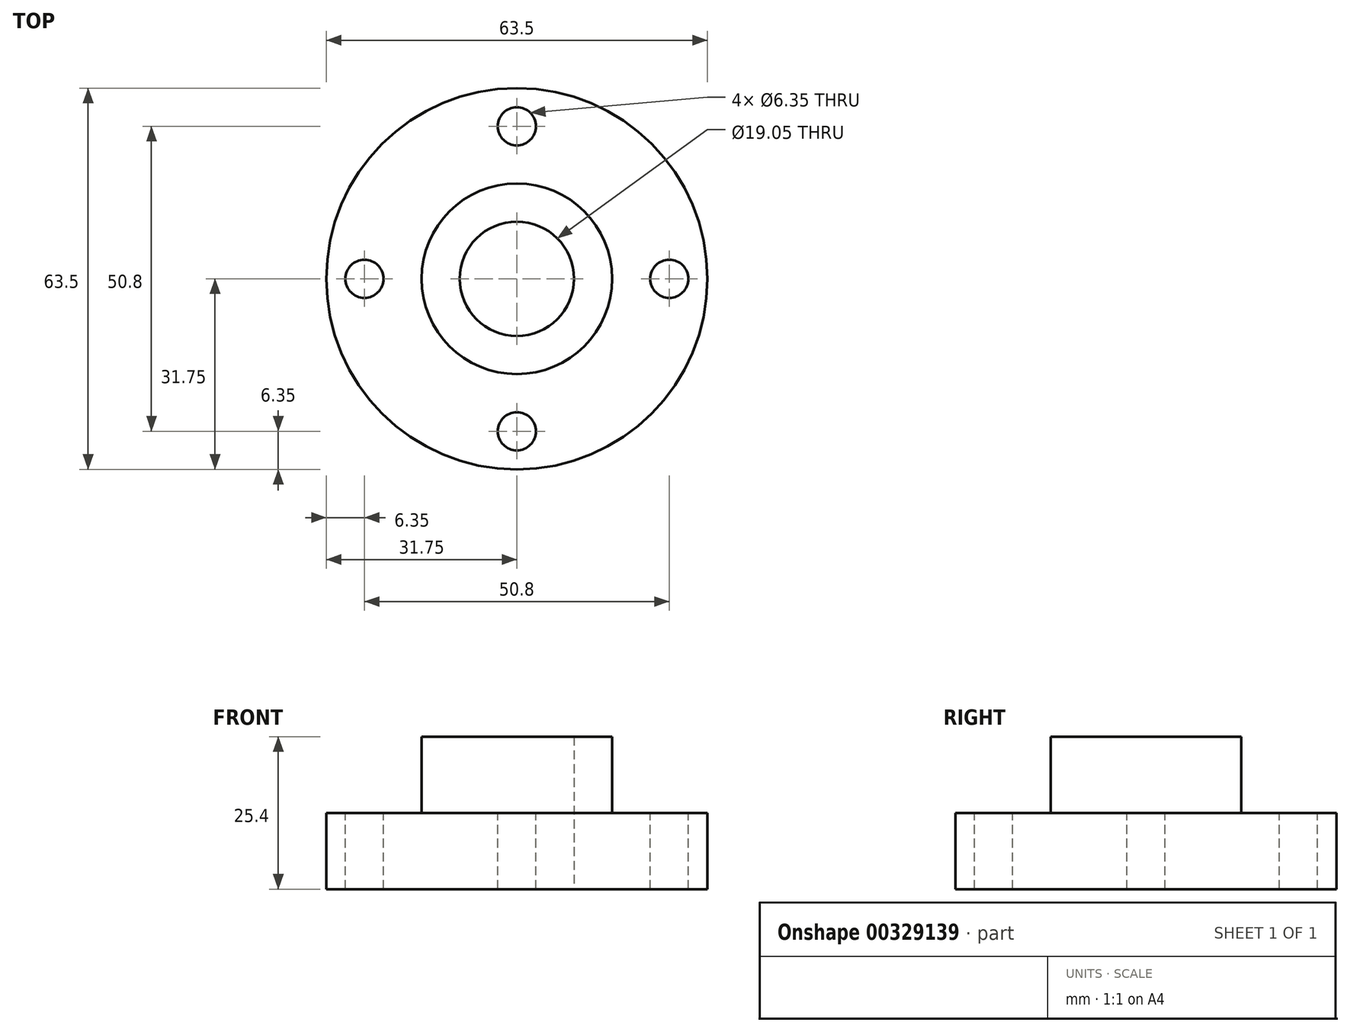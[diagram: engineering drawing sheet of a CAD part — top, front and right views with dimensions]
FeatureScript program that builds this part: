
annotation { "Feature Type Name" : "Feature", "Feature Type Description" : "" }
export const myFeature = defineFeature(function(context is Context, id is Id, definition is map)
    precondition{}
    {
        {
            var Q0;
            Q0=qCreatedBy(makeId("Top.planeOp"),FACE);
            var sketch = newSketch(context, id + "F0", { "sketchPlane" : qUnion([Q0])});
            skCircle(sketch, "E0", {"center": v(0, 0) * mm, "radius": 9.53 * mm});
            skCircle(sketch, "E1", {"center": v(0, 0) * mm, "radius": 15.88 * mm});
            skCircle(sketch, "E2", {"center": v(0, 0) * mm, "radius": 31.75 * mm});
            skSolve(sketch);
        }
        {
            var Q0;
            Q0=makeQuery(id+"F0.imprint","IMPRINT",FACE,{"disambiguationData":[TD([[makeQuery(id+"F0.imprint","IMPRINT",EDGE,{"derivedFrom":sQuery(id+"F0.wireOp",EDGE,"E0")}),-1.0]])]});
            extrude(context, id + "F1", {"entities" : qUnion([Q0]), "depth" : 25.4 * mm});
        }
        {
            var Q0;
            Q0=makeQuery(id+"F0.imprint","IMPRINT",FACE,{"disambiguationData":[TD([[makeQuery(id+"F0.imprint","IMPRINT",EDGE,{"derivedFrom":sQuery(id+"F0.wireOp",EDGE,"E1")}),-1.0]])]});
            extrude(context, id + "F2", {"entities" : qUnion([Q0]), "operationType" : NewBodyOperationType.ADD, "depth" : 12.7 * mm});
        }
        {
            var Q0;
            Q0=makeQuery(id+"F2.opExtrude","CAP_FACE",FACE,{"disambiguationData":[OSD([sQuery(id+"F0.wireOp",EDGE,"E1"),sQuery(id+"F0.wireOp",EDGE,"E2")])],"isStart":false});
            var sketch = newSketch(context, id + "F3", { "sketchPlane" : qUnion([Q0])});
            skCircle(sketch, "E3", {"center": v(-25.4, 0) * mm, "radius": 3.18 * mm});
            skCircle(sketch, "E4", {"center": v(0, -25.4) * mm, "radius": 3.18 * mm});
            skCircle(sketch, "E5", {"center": v(25.4, 0) * mm, "radius": 3.18 * mm});
            skCircle(sketch, "E6", {"center": v(0, 25.4) * mm, "radius": 3.18 * mm});
            skSolve(sketch);
        }
        {
            var Q0;
            Q0=makeQuery(id+"F3.imprint","IMPRINT",FACE,{"disambiguationData":[TD([[makeQuery(id+"F3.imprint","IMPRINT",EDGE,{"derivedFrom":sQuery(id+"F3.wireOp",EDGE,"E6")}),1.0]])]});
            var Q1;
            Q1=makeQuery(id+"F3.imprint","IMPRINT",FACE,{"disambiguationData":[TD([[makeQuery(id+"F3.imprint","IMPRINT",EDGE,{"derivedFrom":sQuery(id+"F3.wireOp",EDGE,"E5")}),1.0]])]});
            var Q2;
            Q2=makeQuery(id+"F3.imprint","IMPRINT",FACE,{"disambiguationData":[TD([[makeQuery(id+"F3.imprint","IMPRINT",EDGE,{"derivedFrom":sQuery(id+"F3.wireOp",EDGE,"E4")}),1.0]])]});
            var Q3;
            Q3=makeQuery(id+"F3.imprint","IMPRINT",FACE,{"disambiguationData":[TD([[makeQuery(id+"F3.imprint","IMPRINT",EDGE,{"derivedFrom":sQuery(id+"F3.wireOp",EDGE,"E3")}),1.0]])]});
            extrude(context, id + "F4", {"entities" : qUnion([Q0, Q1, Q2, Q3]), "operationType" : NewBodyOperationType.REMOVE, "endBound" : BoundingType.THROUGH_ALL, "oppositeDirection" : true, "depth" : 25.4 * mm});
        }
    });
